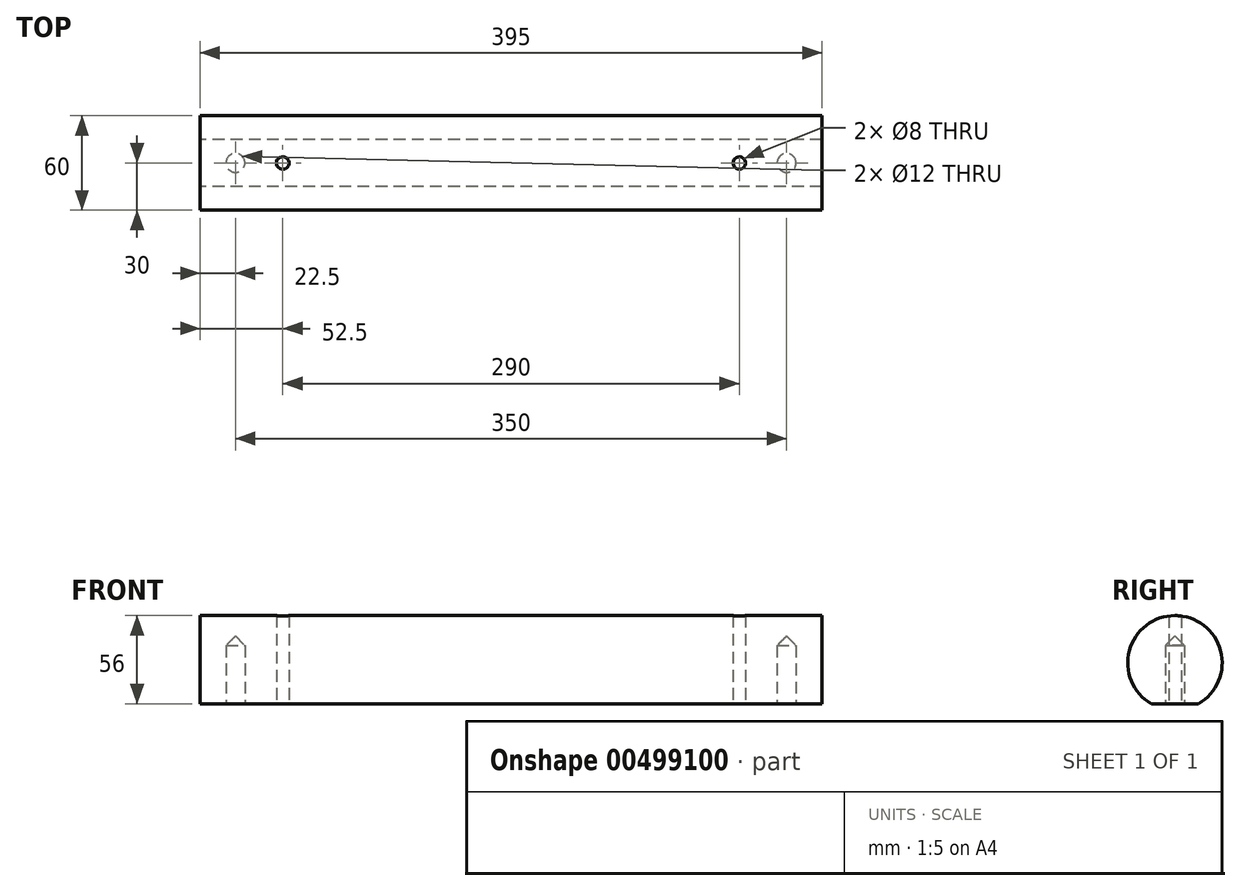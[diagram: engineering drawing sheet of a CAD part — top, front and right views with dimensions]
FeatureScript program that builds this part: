
annotation { "Feature Type Name" : "Feature", "Feature Type Description" : "" }
export const myFeature = defineFeature(function(context is Context, id is Id, definition is map)
    precondition{}
    {
        {
            var Q0;
            Q0=qCreatedBy(makeId("Right.planeOp"),FACE);
            var sketch = newSketch(context, id + "F0", { "sketchPlane" : qUnion([Q0])});
            skArc(sketch, "E0", {"start": v(14.97, -26) * mm, "mid": v(0, 30) * mm, "end": v(-14.97, -26) * mm});
            skLineSegment(sketch, "E1", {"start": v(-14.97, -26) * mm, "end": v(14.97, -26) * mm});
            skSolve(sketch);
        }
        {
            var Q0;
            Q0 = qSketchRegion(id + "F0", true);
            extrude(context, id + "F1", {"entities" : qUnion([Q0]), "depth" : 395 * mm});
        }
        {
            var Q0;
            Q0=makeQuery(id+"F1.opExtrude","SWEPT_FACE",FACE,{"disambiguationData":[OSD([sQuery(id+"F0.wireOp",EDGE,"E1")])]});
            var sketch = newSketch(context, id + "F2", { "sketchPlane" : qUnion([Q0])});
            skCircle(sketch, "E2", {"center": v(372.5, 0) * mm, "radius": 6 * mm});
            skCircle(sketch, "E3", {"center": v(22.5, 0) * mm, "radius": 6 * mm});
            skCircle(sketch, "E4", {"center": v(52.5, 0) * mm, "radius": 4 * mm});
            skCircle(sketch, "E5", {"center": v(342.5, 0) * mm, "radius": 4 * mm});
            skSolve(sketch);
        }
        {
            var Q0;
            Q0 = qSketchRegion(id + "F2", true);
            extrude(context, id + "F3", {"entities" : qUnion([Q0]), "operationType" : NewBodyOperationType.REMOVE, "oppositeDirection" : true, "depth" : 43 * mm});
        }
        {
            var Q0;
            Q0=makeQuery(id+"F1.opExtrude","SWEPT_FACE",FACE,{"disambiguationData":[OSD([sQuery(id+"F0.wireOp",EDGE,"E1")])]});
            var sketch = newSketch(context, id + "F4", { "sketchPlane" : qUnion([Q0])});
            skCircle(sketch, "E6", {"center": v(52.5, 0) * mm, "radius": 4 * mm});
            skCircle(sketch, "E7", {"center": v(342.5, 0) * mm, "radius": 4 * mm});
            skSolve(sketch);
        }
        {
            var Q0;
            Q0 = qSketchRegion(id + "F4", true);
            extrude(context, id + "F5", {"entities" : qUnion([Q0]), "operationType" : NewBodyOperationType.REMOVE, "oppositeDirection" : true, "depth" : 71 * mm});
        }
        {
            var Q0;
            Q0=makeQuery(id+"F3.boolean.opBoolean","COPY",EDGE,{"derivedFrom":makeQuery(id+"F3.opExtrude","CAP_EDGE",EDGE,{"disambiguationData":[OSD([sQuery(id+"F2.wireOp",EDGE,"E2")])],"isStart":false})});
            var Q1;
            Q1=makeQuery(id+"F3.boolean.opBoolean","COPY",EDGE,{"derivedFrom":makeQuery(id+"F3.opExtrude","CAP_EDGE",EDGE,{"disambiguationData":[OSD([sQuery(id+"F2.wireOp",EDGE,"E3")])],"isStart":false})});
            chamfer(context, id + "F6", {"entities" : qUnion([Q0, Q1]), "width" : 6 * mm, "tangentPropagation" : true});
        }
    });
